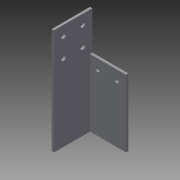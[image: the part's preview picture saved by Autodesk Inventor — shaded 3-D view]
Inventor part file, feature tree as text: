
AUTODESK INVENTOR PART (.ipt)
format: ipt  version: 2015 SP1 (Build 190203100, 203)  size: 111,616 bytes
history: native  units: in
note: dims shown in document units (in); Inventor stores cm internally (conversion verified against a paired STEP export)
features: sketch x4, projected_geometry x3, extrude x2, hole x2
ambient origin geometry x8: Origin, YZ Plane, XZ Plane, XY Plane, X Axis, Y Axis, Z Axis, Center Point
bodies: Solid1 (feature_tree)
feature tree (11):
  extrude  "Extrusion1"  Depth=2.0in
  hole  "Hole1"  [1 undecoded]
  hole  "Hole2"  [1 undecoded]
  extrude  "Extrusion2"  Depth=2.0in
  sketch  "Sketch1"  dims[d0=0.125in d1=2.0in]
  sketch  "Sketch2"  dims[d2=2.0in d3=0.125in]
  projected_geometry  "Projected Loop1"
  sketch  "Sketch3"  dims[d4=5.25in d5=0.0in d6=0.5in]
  projected_geometry  "Projected Loop2"
  sketch  "Sketch4"  dims[d7=0.5in d8=0.5in d9=0.5in d10=0.5in d11=1.5in d12=0.5in d13=1.5in d14=0.25in d15=0.75in d16=0.375in d17=0.25in d18=0.5635in d19=1.0in d20=0.8108in d21=0.5in d22=0.5in d23=2.5in d24=2.5in d25=0.25in d26=0.75in d27=0.375in d28=0.25in d29=0.5635in d30=1.0in d31=0.8108in d32=2.0in d33=0.0in]
  projected_geometry  "Projected Loop3"
note: 2 required parameter values undecoded (feature->parameter linkage not recoverable at this tier; creation-order binding heuristic only, values carry confidence <= 0.55)
